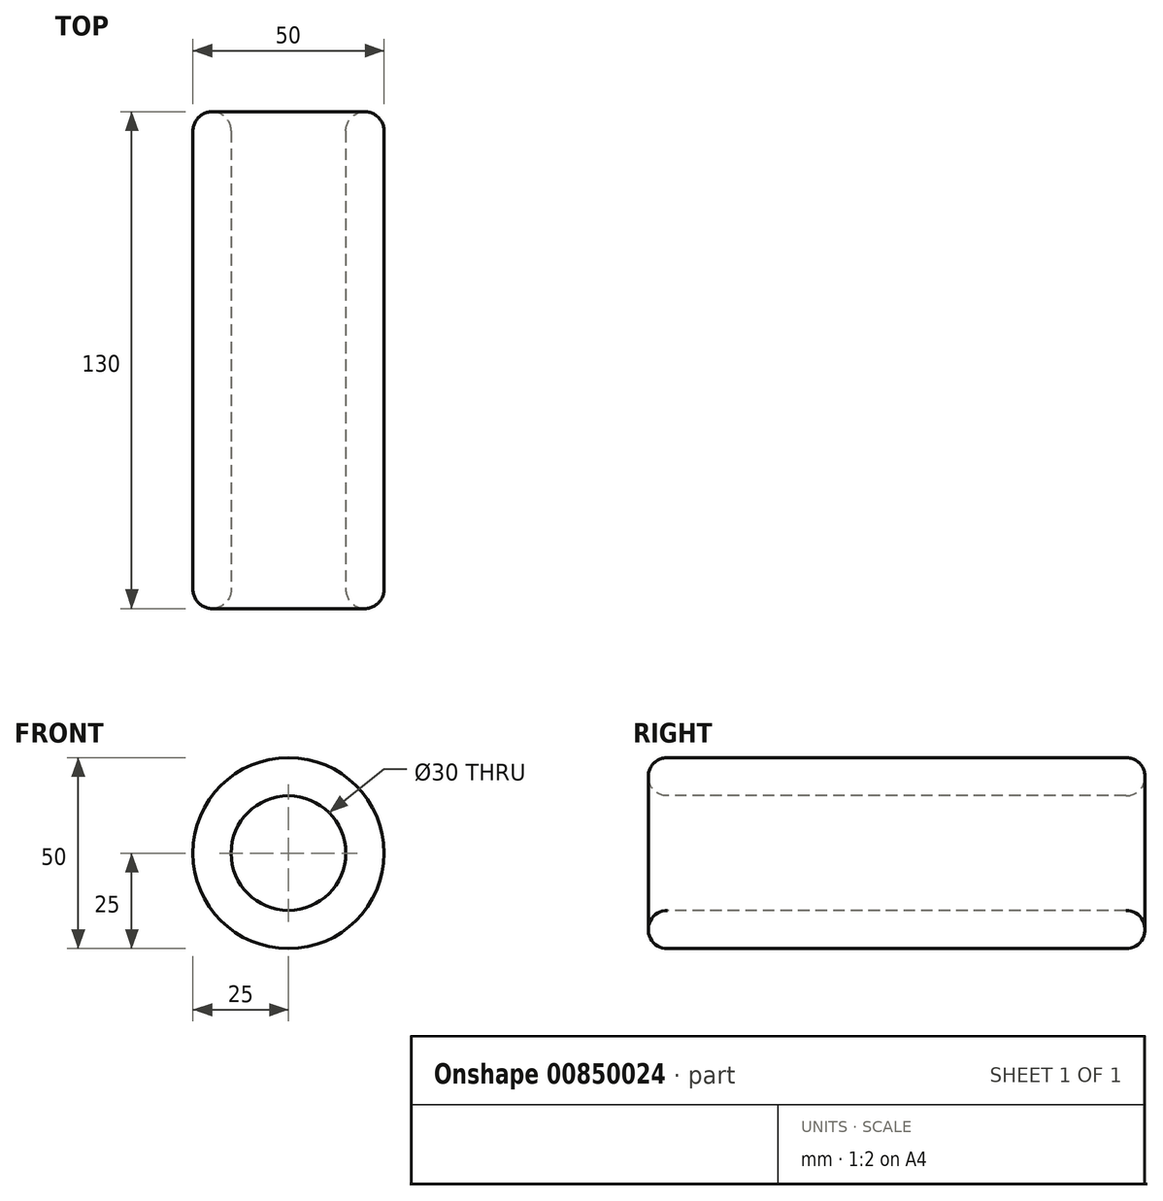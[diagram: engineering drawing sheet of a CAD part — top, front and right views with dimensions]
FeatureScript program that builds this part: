
annotation { "Feature Type Name" : "Feature", "Feature Type Description" : "" }
export const myFeature = defineFeature(function(context is Context, id is Id, definition is map)
    precondition{}
    {
        {
            var Q0;
            Q0=qCreatedBy(makeId("Front.planeOp"),FACE);
            var sketch = newSketch(context, id + "F0", { "sketchPlane" : qUnion([Q0])});
            skCircle(sketch, "E0", {"center": v(0, 0) * mm, "radius": 15 * mm});
            skCircle(sketch, "E1", {"center": v(0, 0) * mm, "radius": 25 * mm});
            skSolve(sketch);
        }
        {
            var Q0;
            Q0=makeQuery(id+"F0.imprint","IMPRINT",FACE,{"disambiguationData":[TD([[makeQuery(id+"F0.imprint","IMPRINT",EDGE,{"derivedFrom":sQuery(id+"F0.wireOp",EDGE,"E0")}),-1.0]])]});
            extrude(context, id + "F1", {"entities" : qUnion([Q0]), "oppositeDirection" : true, "depth" : 130 * mm, "offsetDistance" : 25 * mm});
        }
        {
            var Q0;
            Q0=makeQuery(id+"F1.opExtrude","CAP_EDGE",EDGE,{"disambiguationData":[OSD([sQuery(id+"F0.wireOp",EDGE,"E0")])],"isStart":true});
            var Q1;
            Q1=makeQuery(id+"F1.opExtrude","CAP_EDGE",EDGE,{"disambiguationData":[OSD([sQuery(id+"F0.wireOp",EDGE,"E1")])],"isStart":true});
            var Q2;
            Q2=makeQuery(id+"F1.opExtrude","SWEPT_FACE",FACE,{"disambiguationData":[OSD([sQuery(id+"F0.wireOp",EDGE,"E1")])]});
            var Q3;
            Q3=makeQuery(id+"F1.opExtrude","CAP_EDGE",EDGE,{"disambiguationData":[OSD([sQuery(id+"F0.wireOp",EDGE,"E0")])],"isStart":false});
            fillet(context, id + "F2", {"entities" : qUnion([Q0, Q1, Q2, Q3]), "radius" : 5 * mm, "tangentPropagation" : true, "allowEdgeOverflow" : false});
        }
    });
